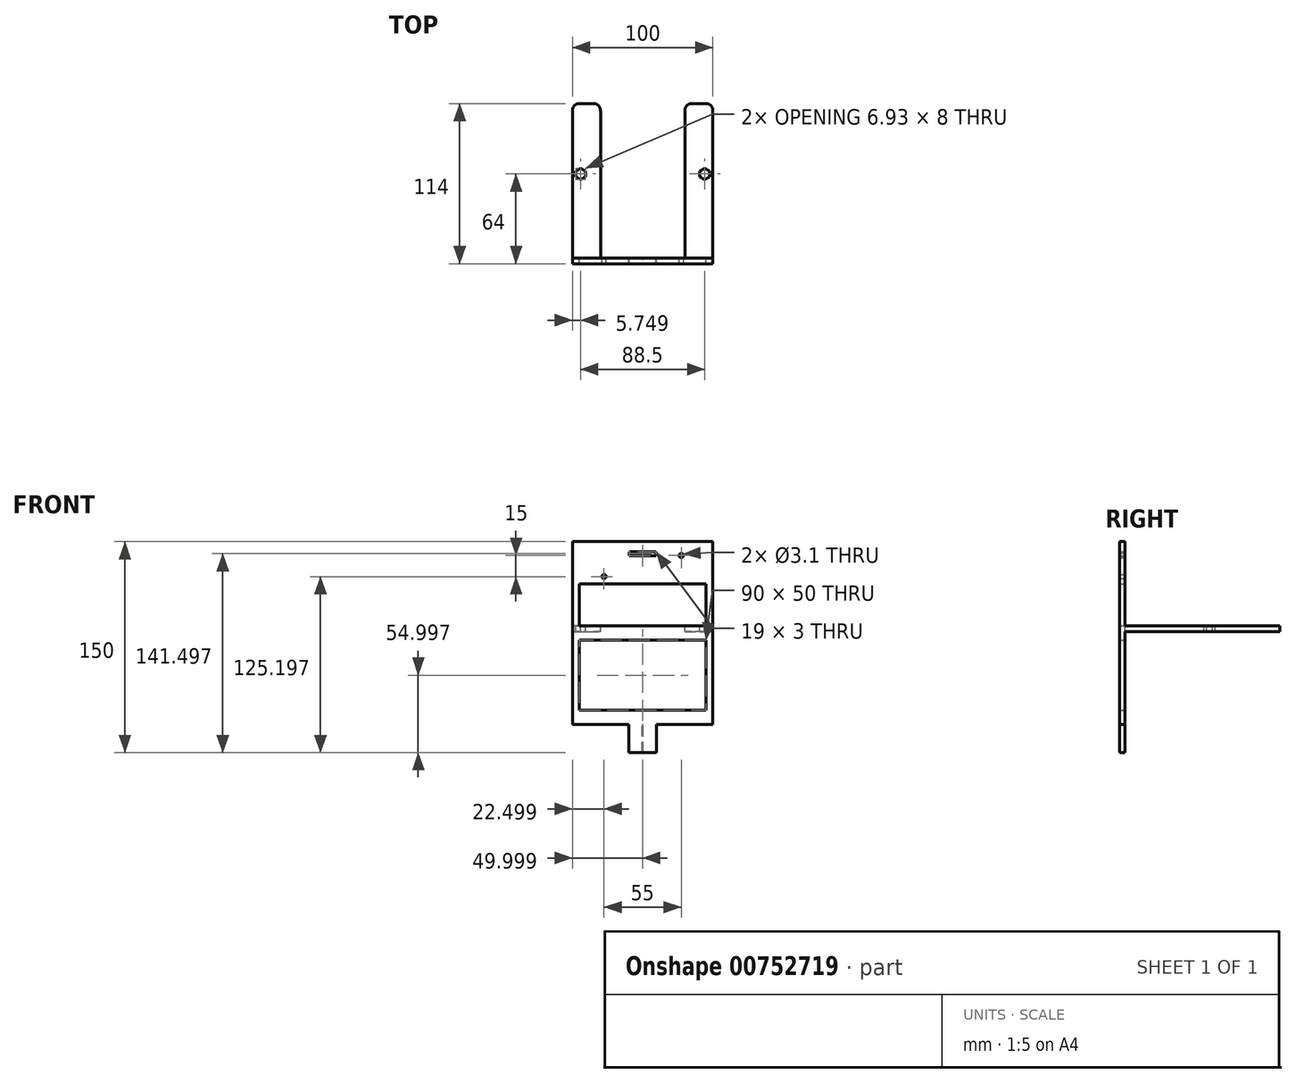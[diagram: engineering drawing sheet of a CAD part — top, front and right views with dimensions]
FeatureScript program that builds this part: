
annotation { "Feature Type Name" : "Feature", "Feature Type Description" : "" }
export const myFeature = defineFeature(function(context is Context, id is Id, definition is map)
    precondition{}
    {
        {
            var Q0;
            Q0=qCreatedBy(makeId("Front.planeOp"),FACE);
            var sketch = newSketch(context, id + "F0", { "sketchPlane" : qUnion([Q0])});
            skLineSegment(sketch, "E0.bottom", {"start": v(-49.14, 66.16) * mm, "end": v(50.86, 66.16) * mm});
            skLineSegment(sketch, "E0.top", {"start": v(-49.14, -83.84) * mm, "end": v(50.86, -83.84) * mm});
            skLineSegment(sketch, "E0.left", {"start": v(-49.14, 66.16) * mm, "end": v(-49.14, -83.84) * mm});
            skLineSegment(sketch, "E0.right", {"start": v(50.86, 66.16) * mm, "end": v(50.86, -83.84) * mm});
            skLineSegment(sketch, "E1.bottom", {"start": v(50.86, -83.84) * mm, "end": v(10.86, -83.84) * mm});
            skLineSegment(sketch, "E1.top", {"start": v(50.86, -63.84) * mm, "end": v(10.86, -63.84) * mm});
            skLineSegment(sketch, "E1.left", {"start": v(50.86, -83.84) * mm, "end": v(50.86, -63.84) * mm});
            skLineSegment(sketch, "E1.right", {"start": v(10.86, -83.84) * mm, "end": v(10.86, -63.84) * mm});
            skLineSegment(sketch, "E2.bottom", {"start": v(-49.14, -83.84) * mm, "end": v(-9.14, -83.84) * mm});
            skLineSegment(sketch, "E2.top", {"start": v(-49.14, -63.84) * mm, "end": v(-9.14, -63.84) * mm});
            skLineSegment(sketch, "E2.left", {"start": v(-49.14, -83.84) * mm, "end": v(-49.14, -63.84) * mm});
            skLineSegment(sketch, "E2.right", {"start": v(-9.14, -83.84) * mm, "end": v(-9.14, -63.84) * mm});
            skLineSegment(sketch, "E3.bottom", {"start": v(-44.14, -3.84) * mm, "end": v(45.86, -3.84) * mm});
            skLineSegment(sketch, "E3.top", {"start": v(-44.14, -53.84) * mm, "end": v(45.86, -53.84) * mm});
            skLineSegment(sketch, "E3.left", {"start": v(-44.14, -3.84) * mm, "end": v(-44.14, -53.84) * mm});
            skLineSegment(sketch, "E3.right", {"start": v(45.86, -3.84) * mm, "end": v(45.86, -53.84) * mm});
            skLineSegment(sketch, "E4.bottom", {"start": v(-44.14, 36.16) * mm, "end": v(45.86, 36.16) * mm});
            skLineSegment(sketch, "E4.top", {"start": v(-44.14, 6.16) * mm, "end": v(45.86, 6.16) * mm});
            skLineSegment(sketch, "E4.left", {"start": v(-44.14, 36.16) * mm, "end": v(-44.14, 6.16) * mm});
            skLineSegment(sketch, "E4.right", {"start": v(45.86, 36.16) * mm, "end": v(45.86, 6.16) * mm});
            skLineSegment(sketch, "E5.bottom", {"start": v(10.36, 56.16) * mm, "end": v(-8.64, 56.16) * mm});
            skLineSegment(sketch, "E5.top", {"start": v(10.36, 59.16) * mm, "end": v(-8.64, 59.16) * mm});
            skLineSegment(sketch, "E5.left", {"start": v(10.36, 56.16) * mm, "end": v(10.36, 59.16) * mm});
            skLineSegment(sketch, "E5.right", {"start": v(-8.64, 56.16) * mm, "end": v(-8.64, 59.16) * mm});
            skCircle(sketch, "E6", {"center": v(28.36, 56.36) * mm, "radius": 1.55 * mm});
            skCircle(sketch, "E7", {"center": v(-26.64, 41.36) * mm, "radius": 1.55 * mm});
            skSolve(sketch);
        }
        {
            var Q0;
            Q0=makeQuery(id+"F0.imprint","IMPRINT",FACE,{"disambiguationData":[TD([[makeQuery(id+"F0.imprint","IMPRINT",EDGE,{"derivedFrom":sQuery(id+"F0.wireOp",EDGE,"E0.bottom")}),-1.0]])]});
            extrude(context, id + "F1", {"entities" : qUnion([Q0]), "depth" : 4 * mm, "offsetDistance" : 25 * mm});
        }
        {
            var Q0;
            Q0=makeQuery(id+"F1.opExtrude","SWEPT_FACE",FACE,{"disambiguationData":[OSD([sQuery(id+"F0.wireOp",EDGE,"E4.top")])]});
            var sketch = newSketch(context, id + "F2", { "sketchPlane" : qUnion([Q0])});
            skLineSegment(sketch, "E8.0", {"start": v(-49.14, 0) * mm, "end": v(50.86, 0) * mm});
            skLineSegment(sketch, "E9.bottom", {"start": v(-49.14, 0) * mm, "end": v(-29.14, 0) * mm});
            skLineSegment(sketch, "E9.top", {"start": v(-44.14, 110) * mm, "end": v(-34.14, 110) * mm});
            skLineSegment(sketch, "E9.left", {"start": v(-49.14, 0) * mm, "end": v(-49.14, 105) * mm});
            skLineSegment(sketch, "E9.right", {"start": v(-29.14, 0) * mm, "end": v(-29.14, 105) * mm});
            skLineSegment(sketch, "E10.bottom", {"start": v(45.86, 110) * mm, "end": v(35.86, 110) * mm});
            skLineSegment(sketch, "E10.top", {"start": v(50.86, 0) * mm, "end": v(30.86, 0) * mm});
            skLineSegment(sketch, "E10.left", {"start": v(50.86, 105) * mm, "end": v(50.86, 0) * mm});
            skLineSegment(sketch, "E10.right", {"start": v(30.86, 105) * mm, "end": v(30.86, 0) * mm});
            skPoint(sketch, "E11.visualSharp", {"position": v(-49.14, 110) * mm});
            skArc(sketch, "E11.filletArc", {"start": v(-44.14, 110) * mm, "mid": v(-47.68, 108.54) * mm, "end": v(-49.14, 105) * mm});
            skPoint(sketch, "E12.visualSharp", {"position": v(-29.14, 110) * mm});
            skArc(sketch, "E12.filletArc", {"start": v(-29.14, 105) * mm, "mid": v(-30.6, 108.54) * mm, "end": v(-34.14, 110) * mm});
            skPoint(sketch, "E13.visualSharp", {"position": v(50.86, 110) * mm});
            skArc(sketch, "E13.filletArc", {"start": v(50.86, 105) * mm, "mid": v(49.4, 108.54) * mm, "end": v(45.86, 110) * mm});
            skPoint(sketch, "E14.visualSharp", {"position": v(30.86, 110) * mm});
            skArc(sketch, "E14.filletArc", {"start": v(35.86, 110) * mm, "mid": v(32.32, 108.54) * mm, "end": v(30.86, 105) * mm});
            skCircle(sketch, "E15.cCircle", {"center": v(-43.4, 60) * mm, "radius": 3.46 * mm, "construction": true});
            skLineSegment(sketch, "E15.0", {"start": v(-43.4, 64) * mm, "end": v(-39.93, 62) * mm});
            skLineSegment(sketch, "E15.1", {"start": v(-39.93, 62) * mm, "end": v(-39.93, 58) * mm});
            skLineSegment(sketch, "E15.2", {"start": v(-39.93, 58) * mm, "end": v(-43.4, 56) * mm});
            skLineSegment(sketch, "E15.3", {"start": v(-43.4, 56) * mm, "end": v(-46.85, 58) * mm});
            skLineSegment(sketch, "E15.4", {"start": v(-46.85, 58) * mm, "end": v(-46.85, 62) * mm});
            skLineSegment(sketch, "E15.5", {"start": v(-46.85, 62) * mm, "end": v(-43.4, 64) * mm});
            skPoint(sketch, "E15.0.midPoint", {"position": v(-41.66, 63) * mm});
            skLineSegment(sketch, "E16", {"start": v(0.86, -4) * mm, "end": v(0.86, 92.09) * mm, "construction": true});
            skCircle(sketch, "E17.MirrorC", {"center": v(45.1, 60) * mm, "radius": 3.46 * mm, "construction": true});
            skLineSegment(sketch, "E18.MirrorCS", {"start": v(48.57, 62) * mm, "end": v(45.1, 64) * mm});
            skLineSegment(sketch, "E19.MirrorCS", {"start": v(45.1, 64) * mm, "end": v(41.65, 62) * mm});
            skLineSegment(sketch, "E20.MirrorCS", {"start": v(41.65, 62) * mm, "end": v(41.65, 58) * mm});
            skLineSegment(sketch, "E21.MirrorCS", {"start": v(41.65, 58) * mm, "end": v(45.1, 56) * mm});
            skLineSegment(sketch, "E22.MirrorCS", {"start": v(45.1, 56) * mm, "end": v(48.57, 58) * mm});
            skLineSegment(sketch, "E23.MirrorCS", {"start": v(48.57, 58) * mm, "end": v(48.57, 62) * mm});
            skSolve(sketch);
        }
        {
            var Q0;
            Q0 = qSketchRegion(id + "F2", true);
            extrude(context, id + "F3", {"entities" : qUnion([Q0]), "operationType" : NewBodyOperationType.ADD, "oppositeDirection" : true, "depth" : 4 * mm, "offsetDistance" : 25 * mm});
        }
        {
            var Q0;
            {var subQ0=sQuery(id+"F0.wireOp",EDGE,"E3.left");var subQ13=sQuery(id+"F0.wireOp",EDGE,"E3.top");var subQ14=sQuery(id+"F0.wireOp",EDGE,"E3.bottom");var subQ15=sQuery(id+"F0.wireOp",EDGE,"E2.right");var subQ17=sQuery(id+"F0.wireOp",EDGE,"E2.top");var subQ19=sQuery(id+"F0.wireOp",EDGE,"E1.right");var subQ20=sQuery(id+"F0.wireOp",EDGE,"E0.top");var subQ21=sQuery(id+"F0.wireOp",EDGE,"E0.left");var subQ22=sQuery(id+"F0.wireOp",EDGE,"E0.right");var subQ33=sQuery(id+"F0.wireOp",EDGE,"E1.top");var subQ34=sQuery(id+"F0.wireOp",EDGE,"E3.right");var subQ35=sQuery(id+"F0.wireOp",EDGE,"E4.top");Q0=makeQuery(id+"F3.boolean.opBoolean","SPLIT",FACE,{"disambiguationData":[TD([makeQuery(id+"F1.opExtrude","SWEPT_FACE",FACE,{"disambiguationData":[OSD([subQ20])]})])],"derivedFrom":makeQuery(id+"F1.opExtrude","CAP_FACE",FACE,{"disambiguationData":[OSD([sQuery(id+"F0.wireOp",EDGE,"E0.bottom"),subQ20,subQ21,subQ22,subQ33,subQ19,subQ17,subQ15,subQ14,subQ13,subQ0,subQ34,sQuery(id+"F0.wireOp",EDGE,"E4.bottom"),subQ35,sQuery(id+"F0.wireOp",EDGE,"E4.left"),sQuery(id+"F0.wireOp",EDGE,"E4.right"),sQuery(id+"F0.wireOp",EDGE,"E5.bottom"),sQuery(id+"F0.wireOp",EDGE,"E5.top"),sQuery(id+"F0.wireOp",EDGE,"E5.left"),sQuery(id+"F0.wireOp",EDGE,"E5.right"),sQuery(id+"F0.wireOp",EDGE,"E6"),sQuery(id+"F0.wireOp",EDGE,"E7")])],"isStart":true})});}
            var sketch = newSketch(context, id + "F4", { "sketchPlane" : qUnion([Q0])});
            skLineSegment(sketch, "E24.bottom", {"start": v(-1.1, -53.84) * mm, "end": v(-0.6, -53.84) * mm});
            skLineSegment(sketch, "E24.top", {"start": v(-1.1, -83.84) * mm, "end": v(-0.6, -83.84) * mm});
            skLineSegment(sketch, "E25.bottom", {"start": v(-0.6, -83.84) * mm, "end": v(-1.1, -83.84) * mm});
            skLineSegment(sketch, "E25.top", {"start": v(-0.6, -63.84) * mm, "end": v(-1.1, -63.84) * mm});
            skLineSegment(sketch, "E25.left", {"start": v(-0.6, -83.84) * mm, "end": v(-0.6, -63.84) * mm});
            skLineSegment(sketch, "E25.right", {"start": v(-1.1, -83.84) * mm, "end": v(-1.1, -63.84) * mm});
            skSolve(sketch);
        }
        {
            var Q0;
            Q0 = qSketchRegion(id + "F4", true);
            extrude(context, id + "F5", {"entities" : qUnion([Q0]), "operationType" : NewBodyOperationType.REMOVE, "oppositeDirection" : true, "depth" : 0.5 * mm, "offsetDistance" : 25 * mm});
        }
    });
